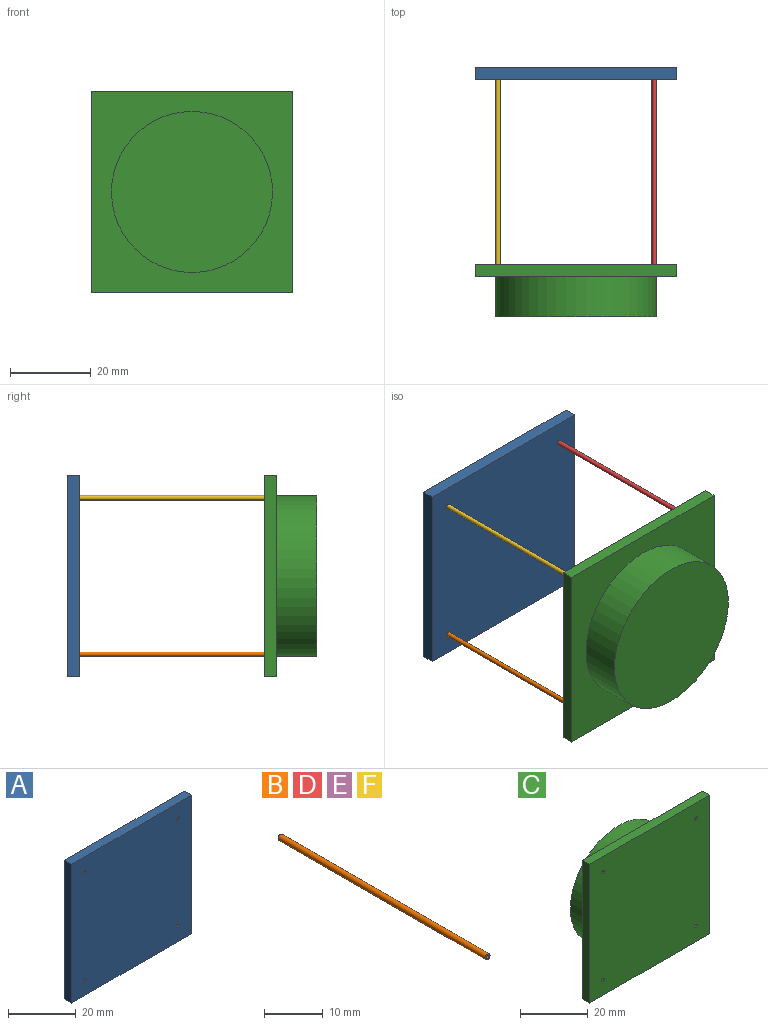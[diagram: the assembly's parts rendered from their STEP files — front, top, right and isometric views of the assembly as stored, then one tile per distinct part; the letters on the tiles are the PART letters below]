
ASSEMBLY  parts=6 mates=5
PART A: 14 faces, bbox 50x3x50 mm
  f0: plane 50x3mm, normal (0,0,1), area 150mm2, adj f1,f3,f4,f5
  f1: plane 50x3mm, normal (-1,0,0), area 150mm2, adj f0,f2,f4,f5
  f2: plane 50x3mm, normal (0,0,-1), area 150mm2, adj f1,f3,f4,f5
  f3: plane 50x3mm, normal (1,0,0), area 150mm2, adj f0,f2,f4,f5
  f4: plane 50x50mm, normal (0,1,0), area 2500mm2, adj f0,f1,f2,f3
  f5: plane 50x50mm, normal (0,-1,0), area 2495.9mm2, adj f0,f1,f2,f3,f6,f8,f10,f12
  f6: cylinder r=0.57mm len=2mm, axis (0,-1,0), area 7.2mm2, adj f5,f7
  f7: plane 1.14x1.14mm, normal (0,-1,0), area 1mm2, adj f6
  f8: cylinder r=0.57mm len=2mm, axis (0,-1,0), area 7.2mm2, adj f5,f9
  f9: plane 1.14x1.14mm, normal (0,-1,0), area 1mm2, adj f8
  f10: cylinder r=0.57mm len=2mm, axis (0,-1,0), area 7.2mm2, adj f5,f11
  f11: plane 1.14x1.14mm, normal (0,-1,0), area 1mm2, adj f10
  f12: cylinder r=0.57mm len=2mm, axis (0,-1,0), area 7.2mm2, adj f5,f13
  f13: plane 1.14x1.14mm, normal (0,-1,0), area 1mm2, adj f12
PART B: 4 faces, bbox 1.1x50x1.1 mm
  f0: cylinder r=0.31mm len=50mm, axis (0,1,0), area 97.4mm2, adj f2,f3
  f1: cylinder r=0.57mm len=50mm, axis (0,1,0), area 179.1mm2, adj f2,f3
  f2: plane 1.14x1.14mm, normal (0,-1,0), area 0.7mm2, adj f0,f1
  f3: plane 1.14x1.14mm, normal (0,1,0), area 0.7mm2, adj f0,f1
PART C: 16 faces, bbox 50x13x50 mm
  f0: plane 50x3mm, normal (0,0,1), area 150mm2, adj f1,f3,f4,f5
  f1: plane 50x3mm, normal (-1,0,0), area 150mm2, adj f0,f2,f4,f5
  f2: plane 50x3mm, normal (0,0,-1), area 150mm2, adj f1,f3,f4,f5
  f3: plane 50x3mm, normal (1,0,0), area 150mm2, adj f0,f2,f4,f5
  f4: plane 50x50mm, normal (0,1,0), area 1243.4mm2, adj f0,f1,f2,f3,f14
  f5: plane 50x50mm, normal (0,-1,0), area 2495.9mm2, adj f0,f1,f2,f3,f6,f8,f10,f12
  f6: cylinder r=0.57mm len=2mm, axis (0,-1,0), area 7.2mm2, adj f5,f7
  f7: plane 1.14x1.14mm, normal (0,-1,0), area 1mm2, adj f6
  f8: cylinder r=0.57mm len=2mm, axis (0,-1,0), area 7.2mm2, adj f5,f9
  f9: plane 1.14x1.14mm, normal (0,-1,0), area 1mm2, adj f8
  f10: cylinder r=0.57mm len=2mm, axis (0,-1,0), area 7.2mm2, adj f5,f11
  f11: plane 1.14x1.14mm, normal (0,-1,0), area 1mm2, adj f10
  f12: cylinder r=0.57mm len=2mm, axis (0,-1,0), area 7.2mm2, adj f5,f13
  f13: plane 1.14x1.14mm, normal (0,-1,0), area 1mm2, adj f12
  f14: cylinder r=20mm len=40mm, axis (0,-1,0), area 1256.6mm2, adj f4,f15
  f15: plane 40x40mm, normal (0,1,0), area 1256.6mm2, adj f14
PART D: same geometry as B
PART E: same geometry as B
PART F: same geometry as B
PLACE A t=(7.07,9.57,-34.35)mm
PLACE B t=(-12.36,11.57,-53.78)mm
PLACE C rot(axis=(0,0,1),180deg) t=(7.07,-36.43,-34.35)mm
PLACE D t=(26.5,11.57,-14.92)mm
PLACE E t=(26.5,11.57,-53.78)mm
PLACE F t=(-12.36,11.57,-14.92)mm
MATE fastened C.f6 <-> D.f1  axis (0,1,0) through (26.5,-38.43,-14.92)mm
MATE fastened A.f10 <-> B.f1  axis (0,-1,0) through (-12.36,11.57,-53.78)mm
MATE fastened C.f8 <-> B.f1  axis (0,1,0) through (-12.36,-38.43,-53.78)mm
MATE fastened C.f10 <-> E.f1  axis (0,1,0) through (26.5,-38.43,-53.78)mm
MATE fastened C.f12 <-> F.f1  axis (0,1,0) through (-12.36,-38.43,-14.92)mm
